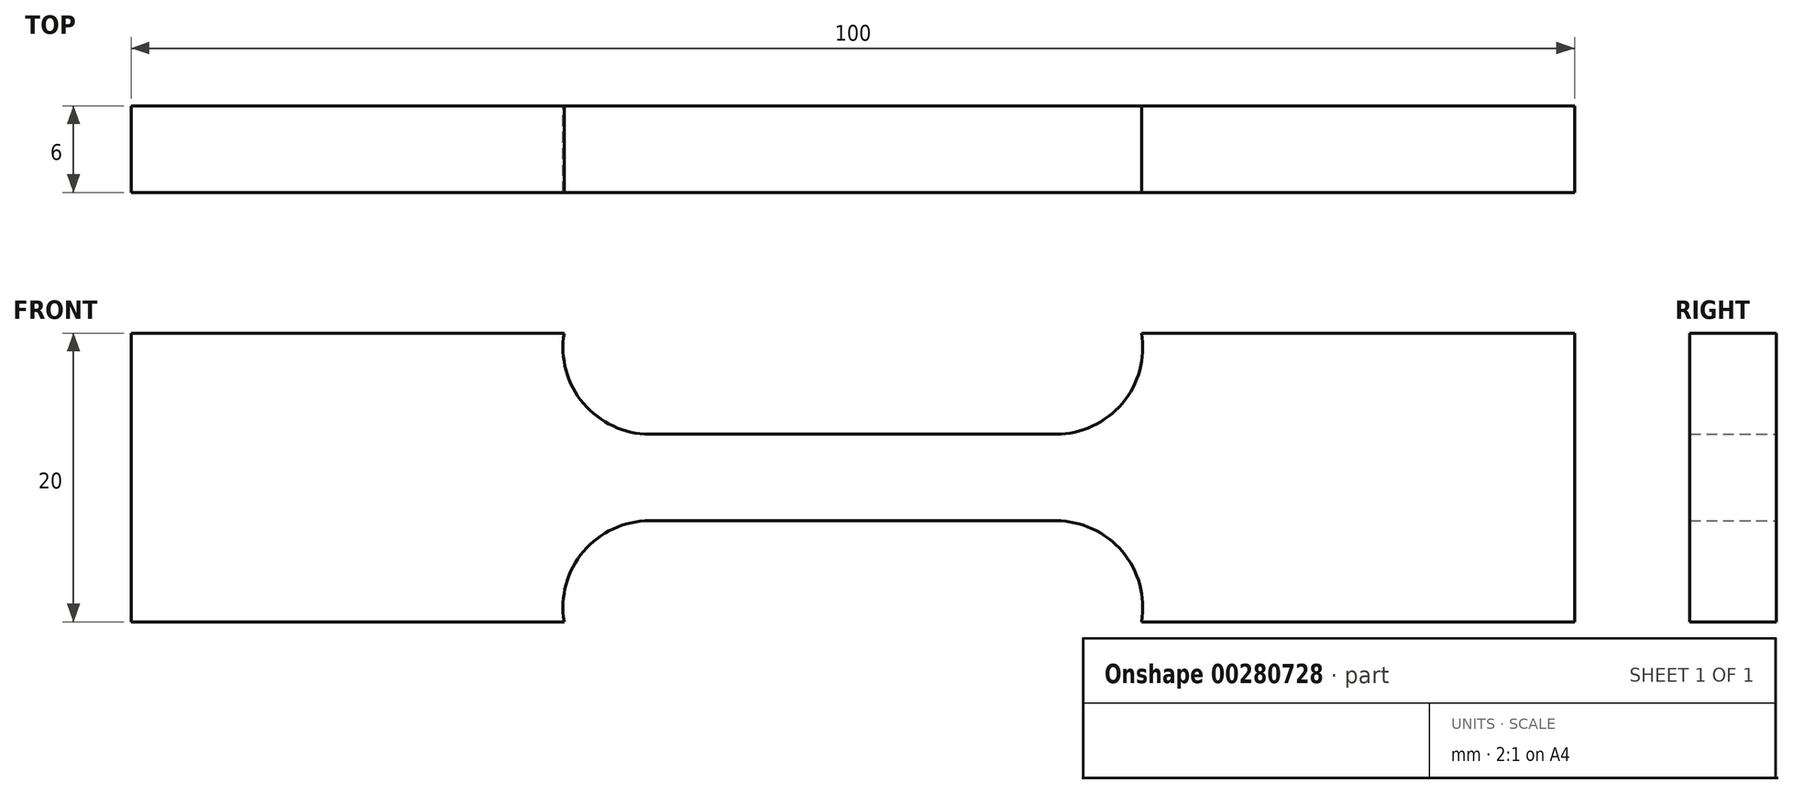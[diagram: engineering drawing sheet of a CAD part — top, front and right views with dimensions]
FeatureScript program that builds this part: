
annotation { "Feature Type Name" : "Feature", "Feature Type Description" : "" }
export const myFeature = defineFeature(function(context is Context, id is Id, definition is map)
    precondition{}
    {
        {
            var Q0;
            Q0=qCreatedBy(makeId("Front.planeOp"),FACE);
            var sketch = newSketch(context, id + "F0", { "sketchPlane" : qUnion([Q0])});
            skLineSegment(sketch, "E0", {"start": v(0, 3) * mm, "end": v(14.08, 3) * mm});
            skArc(sketch, "E1", {"start": v(14.08, 3) * mm, "mid": v(18.67, 5.13) * mm, "end": v(20, 10) * mm});
            skLineSegment(sketch, "E2", {"start": v(20, 10) * mm, "end": v(50, 10) * mm});
            skLineSegment(sketch, "E3.MirrorCS", {"start": v(20, -10) * mm, "end": v(50, -10) * mm});
            skLineSegment(sketch, "E4.MirrorCS", {"start": v(0, -3) * mm, "end": v(14.08, -3) * mm});
            skArc(sketch, "E5.MirrorCS", {"start": v(14.08, -3) * mm, "mid": v(18.67, -5.13) * mm, "end": v(20, -10) * mm});
            skLineSegment(sketch, "E6.MirrorCS", {"start": v(-20, -10) * mm, "end": v(-50, -10) * mm});
            skLineSegment(sketch, "E7.MirrorCS", {"start": v(-20, 10) * mm, "end": v(-50, 10) * mm});
            skArc(sketch, "E8.MirrorCS", {"start": v(-14.08, -3) * mm, "mid": v(-18.67, -5.13) * mm, "end": v(-20, -10) * mm});
            skLineSegment(sketch, "E9.MirrorCS", {"start": v(0, -3) * mm, "end": v(-14.08, -3) * mm});
            skLineSegment(sketch, "E10.MirrorCS", {"start": v(0, 3) * mm, "end": v(-14.08, 3) * mm});
            skArc(sketch, "E11.MirrorCS", {"start": v(-14.08, 3) * mm, "mid": v(-18.67, 5.13) * mm, "end": v(-20, 10) * mm});
            skLineSegment(sketch, "E12", {"start": v(-50, 10) * mm, "end": v(-50, -10) * mm});
            skLineSegment(sketch, "E13", {"start": v(50, 10) * mm, "end": v(50, -10) * mm});
            skSolve(sketch);
        }
        {
            var Q0;
            Q0 = qSketchRegion(id + "F0", true);
            extrude(context, id + "F1", {"entities" : qUnion([Q0]), "depth" : 6 * mm});
        }
    });
